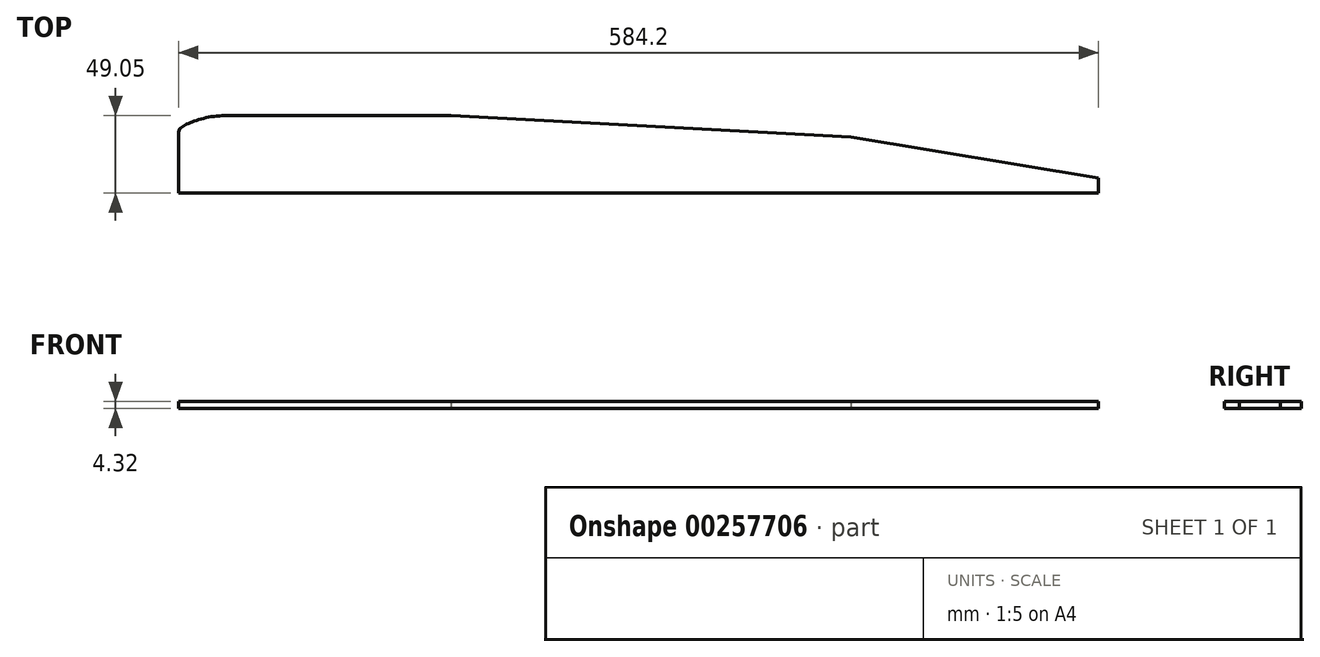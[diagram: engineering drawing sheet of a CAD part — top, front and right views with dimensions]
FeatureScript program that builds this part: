
annotation { "Feature Type Name" : "Feature", "Feature Type Description" : "" }
export const myFeature = defineFeature(function(context is Context, id is Id, definition is map)
    precondition{}
    {
        {
            var Q0;
            Q0=qCreatedBy(makeId("Top.planeOp"),FACE);
            var sketch = newSketch(context, id + "F0", { "sketchPlane" : qUnion([Q0])});
            skLineSegment(sketch, "E0", {"start": v(0, 38.74) * mm, "end": v(0, 0) * mm});
            skLineSegment(sketch, "E1", {"start": v(0, 0) * mm, "end": v(584.2, 0) * mm});
            skLineSegment(sketch, "E2", {"start": v(584.2, 0) * mm, "end": v(584.2, 9.52) * mm});
            skLineSegment(sketch, "E3", {"start": v(584.2, 9.52) * mm, "end": v(426.91, 35.56) * mm});
            skLineSegment(sketch, "E4", {"start": v(426.91, 35.56) * mm, "end": v(172.91, 49.05) * mm});
            skLineSegment(sketch, "E5", {"start": v(172.91, 49.05) * mm, "end": v(29.5, 49.05) * mm});
            skFitSpline(sketch, "E6", {"points": [v(0, 38.74) * mm, v(3.66, 42.83) * mm, v(13.13, 46.64) * mm, v(29.5, 49.05) * mm], "startDerivative": vector(0, 25.08) * mm, "endDerivative": vector(41.17, 0) * mm});
            skPoint(sketch, "E7.orphan", {"position": v(0, -38.74) * mm});
            skSolve(sketch);
        }
        {
            var Q0;
            Q0 = qSketchRegion(id + "F0", true);
            extrude(context, id + "F1", {"entities" : qUnion([Q0]), "depth" : 4.32 * mm});
        }
    });
